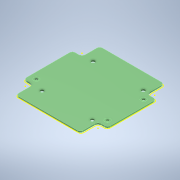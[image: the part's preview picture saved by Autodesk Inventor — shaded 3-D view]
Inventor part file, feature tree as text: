
AUTODESK INVENTOR PART (.ipt)
format: ipt  version: 2021 (Build 250183000, 183)  size: 276,480 bytes
history: native  units: mm
features: sketch x5, other x4, extrude x2, hole x2, fillet x2, reference x1
ambient origin geometry x8: Origin, YZ Plane, XZ Plane, XY Plane, X Axis, Y Axis, Z Axis, Center Point
bodies: Solid1 (feature_tree)
feature tree (16):
  extrude  "Extrusion1"  Depth=95.0mm
  hole  "Hole1"  [1 undecoded]
  extrude  "Extrusion2"  Depth=11.0mm
  fillet  "Fillet1"  Radius=20.0mm
  fillet  "Fillet2"  Radius=20.0mm
  sketch  "Sketch5"  dims[d9=3.0mm d10=6.0mm d11=6.0mm d12=0.1mm d13=90.0deg d14=8.0mm d15=20.594885mm d18=11.0mm d19=20.0mm d21=20.0mm]
  hole  "Hole2"  [1 undecoded]
  sketch  "Sketch1"  dims[d0=95.0mm d1=95.0mm]
  sketch  "Sketch2"  dims[d2=1.6mm d3=0.0mm d7=80.79mm]
  sketch  "Sketch4"  dims[d8=40.942mm]
  reference  "Reference2"
  sketch  "Sketch6"  dims[d22=11.0mm d23=11.0mm d24=20.0mm d25=11.0mm d26=20.0mm d27=1.6mm d28=0.0mm d29=4.0mm d30=3.0mm d31=57.0mm d32=58.0mm d33=4.2mm d34=6.0mm d35=4.0mm d36=2.0mm d37=90.0deg d38=8.0mm d39=20.594885mm d41=3.0mm]
  other  "<userpath>\OneDrive\Dokumenty\GitHub\escape_room_hw_v2\Enclosure\Product.iam"
  other  "Product.iam"
  other  "zp105_105_75jph_tm:1"
  other  "zp105_105_75jph_tm_Temp_6:1"
note: 2 required parameter values undecoded (feature->parameter linkage not recoverable at this tier; creation-order binding heuristic only, values carry confidence <= 0.55)
